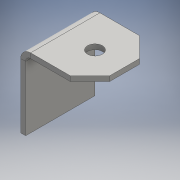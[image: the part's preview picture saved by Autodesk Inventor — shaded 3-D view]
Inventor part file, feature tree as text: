
AUTODESK INVENTOR PART (.ipt)
format: ipt  version: 2016 (Build 200138000, 138)  size: 122,368 bytes
history: native  units: mm
features: sheet_metal_op x4, other x3, sketch x3, hole x1
ambient origin geometry x8: Origin, YZ Plane, XZ Plane, XY Plane, X Axis, Y Axis, Z Axis, Center Point
bodies: Solid1 (feature_tree)
feature tree (11):
  sheet_metal_op  "Face1"
  sheet_metal_op  "Flange1"
  hole  "Hole1"  [1 undecoded]
  other  "Corner Chamfer1"
  sketch  "Sketch1"  dims[d0=14.0mm d1=14.0mm]
  other  "Plate1"
  sketch  "Sketch2"  dims[d2=1.0mm]
  other  "Plate2"
  sheet_metal_op  "Bend1"
  sheet_metal_op  "Corner1"
  sketch  "Sketch3"  dims[d3=1.0mm d4=0.5mm d5=2.0mm d6=1.0mm d7=15.0mm d8=90.0deg d9=1.0mm d10=4.0mm d11=1.0mm d12=1.0mm d13=6.0mm d14=3.0mm d15=6.0mm d16=4.0mm d17=2.0mm d18=90.0deg d19=1.0mm d20=20.594885mm d21=4.0mm d22=6.0mm d23=45.0deg]
note: 1 required parameter value undecoded (feature->parameter linkage not recoverable at this tier; creation-order binding heuristic only, values carry confidence <= 0.55)
